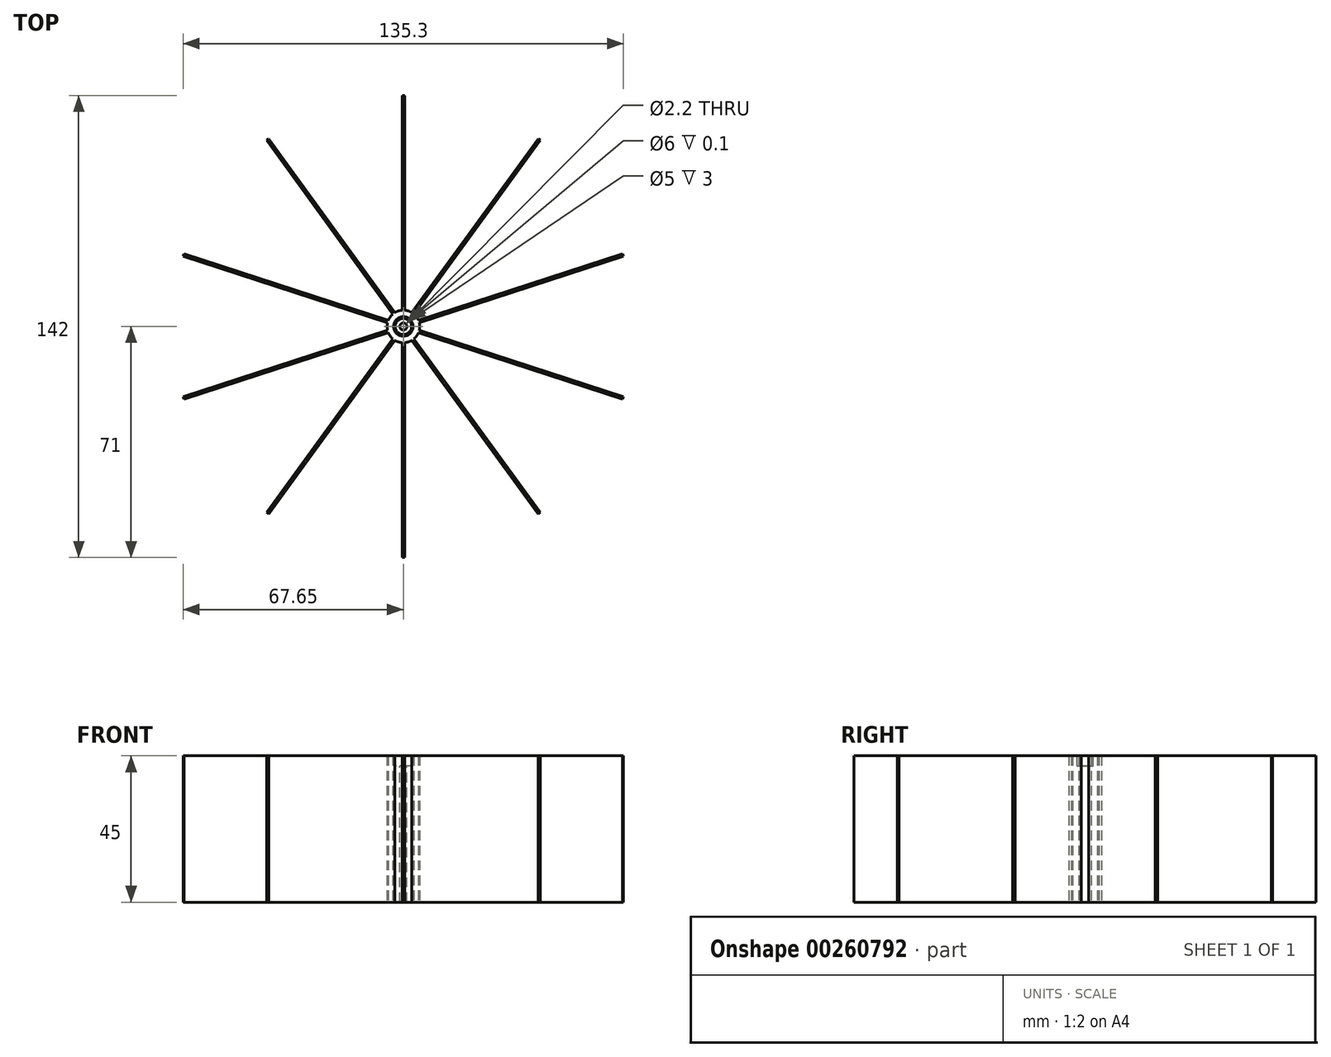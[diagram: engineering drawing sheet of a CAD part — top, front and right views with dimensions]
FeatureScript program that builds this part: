
annotation { "Feature Type Name" : "Feature", "Feature Type Description" : "" }
export const myFeature = defineFeature(function(context is Context, id is Id, definition is map)
    precondition{}
    {
        {
            var Q0;
            Q0=qCreatedBy(makeId("Top.planeOp"),FACE);
            var sketch = newSketch(context, id + "F0", { "sketchPlane" : qUnion([Q0])});
            skCircle(sketch, "E0", {"center": v(0, 0) * mm, "radius": 5 * mm});
            skLineSegment(sketch, "E1.bottom", {"start": v(-0.4, 0) * mm, "end": v(0.4, 0) * mm});
            skLineSegment(sketch, "E1.top", {"start": v(-0.4, 71) * mm, "end": v(0.4, 71) * mm});
            skLineSegment(sketch, "E1.left", {"start": v(-0.4, 0) * mm, "end": v(-0.4, 71) * mm});
            skLineSegment(sketch, "E1.right", {"start": v(0.4, 0) * mm, "end": v(0.4, 71) * mm});
            skLineSegment(sketch, "E2.1.0", {"start": v(-42.06, 57.2) * mm, "end": v(-41.4, 57.68) * mm});
            skLineSegment(sketch, "E2.1.1", {"start": v(-0.32, -0.24) * mm, "end": v(-42.06, 57.2) * mm});
            skLineSegment(sketch, "E2.1.2", {"start": v(0.32, 0.24) * mm, "end": v(-41.4, 57.68) * mm});
            skLineSegment(sketch, "E2.1.3", {"start": v(-0.32, -0.24) * mm, "end": v(0.32, 0.24) * mm});
            skLineSegment(sketch, "E2.2.0", {"start": v(-67.65, 21.56) * mm, "end": v(-67.4, 22.32) * mm});
            skLineSegment(sketch, "E2.2.1", {"start": v(-0.12, -0.38) * mm, "end": v(-67.65, 21.56) * mm});
            skLineSegment(sketch, "E2.2.2", {"start": v(0.12, 0.38) * mm, "end": v(-67.4, 22.32) * mm});
            skLineSegment(sketch, "E2.2.3", {"start": v(-0.12, -0.38) * mm, "end": v(0.12, 0.38) * mm});
            skLineSegment(sketch, "E2.3.0", {"start": v(-67.4, -22.32) * mm, "end": v(-67.65, -21.56) * mm});
            skLineSegment(sketch, "E2.3.1", {"start": v(0.12, -0.38) * mm, "end": v(-67.4, -22.32) * mm});
            skLineSegment(sketch, "E2.3.2", {"start": v(-0.12, 0.38) * mm, "end": v(-67.65, -21.56) * mm});
            skLineSegment(sketch, "E2.3.3", {"start": v(0.12, -0.38) * mm, "end": v(-0.12, 0.38) * mm});
            skLineSegment(sketch, "E2.4.0", {"start": v(-41.4, -57.68) * mm, "end": v(-42.06, -57.2) * mm});
            skLineSegment(sketch, "E2.4.1", {"start": v(0.32, -0.24) * mm, "end": v(-41.4, -57.68) * mm});
            skLineSegment(sketch, "E2.4.2", {"start": v(-0.32, 0.24) * mm, "end": v(-42.06, -57.2) * mm});
            skLineSegment(sketch, "E2.4.3", {"start": v(0.32, -0.24) * mm, "end": v(-0.32, 0.24) * mm});
            skLineSegment(sketch, "E2.5.0", {"start": v(0.4, -71) * mm, "end": v(-0.4, -71) * mm});
            skLineSegment(sketch, "E2.5.1", {"start": v(0.4, 0) * mm, "end": v(0.4, -71) * mm});
            skLineSegment(sketch, "E2.5.2", {"start": v(-0.4, 0) * mm, "end": v(-0.4, -71) * mm});
            skLineSegment(sketch, "E2.5.3", {"start": v(0.4, 0) * mm, "end": v(-0.4, 0) * mm});
            skLineSegment(sketch, "E2.6.0", {"start": v(42.06, -57.2) * mm, "end": v(41.4, -57.68) * mm});
            skLineSegment(sketch, "E2.6.1", {"start": v(0.32, 0.24) * mm, "end": v(42.06, -57.2) * mm});
            skLineSegment(sketch, "E2.6.2", {"start": v(-0.32, -0.24) * mm, "end": v(41.4, -57.68) * mm});
            skLineSegment(sketch, "E2.6.3", {"start": v(0.32, 0.24) * mm, "end": v(-0.32, -0.24) * mm});
            skLineSegment(sketch, "E2.7.0", {"start": v(67.65, -21.56) * mm, "end": v(67.4, -22.32) * mm});
            skLineSegment(sketch, "E2.7.1", {"start": v(0.12, 0.38) * mm, "end": v(67.65, -21.56) * mm});
            skLineSegment(sketch, "E2.7.2", {"start": v(-0.12, -0.38) * mm, "end": v(67.4, -22.32) * mm});
            skLineSegment(sketch, "E2.7.3", {"start": v(0.12, 0.38) * mm, "end": v(-0.12, -0.38) * mm});
            skLineSegment(sketch, "E3.1.8.0", {"start": v(67.4, 22.32) * mm, "end": v(67.65, 21.56) * mm});
            skLineSegment(sketch, "E3.3.8.0", {"start": v(-0.12, 0.38) * mm, "end": v(67.4, 22.32) * mm});
            skLineSegment(sketch, "E3.6.8.0", {"start": v(0.12, -0.38) * mm, "end": v(67.65, 21.56) * mm});
            skLineSegment(sketch, "E3.9.8.0", {"start": v(-0.12, 0.38) * mm, "end": v(0.12, -0.38) * mm});
            skLineSegment(sketch, "E3.1.9.0", {"start": v(41.4, 57.68) * mm, "end": v(42.06, 57.2) * mm});
            skLineSegment(sketch, "E3.3.9.0", {"start": v(-0.32, 0.24) * mm, "end": v(41.4, 57.68) * mm});
            skLineSegment(sketch, "E3.6.9.0", {"start": v(0.32, -0.24) * mm, "end": v(42.06, 57.2) * mm});
            skLineSegment(sketch, "E3.9.9.0", {"start": v(-0.32, 0.24) * mm, "end": v(0.32, -0.24) * mm});
            skSolve(sketch);
        }
        {
            var Q0;
            Q0 = qSketchRegion(id + "F0", true);
            extrude(context, id + "F1", {"entities" : qUnion([Q0]), "depth" : 45 * mm});
        }
        {
            var Q0;
            Q0=makeQuery(id+"F1.opExtrude","CAP_FACE",FACE,{"disambiguationData":[OSD([sQuery(id+"F0.wireOp",EDGE,"E0"),sQuery(id+"F0.wireOp",EDGE,"E1.top"),sQuery(id+"F0.wireOp",EDGE,"E1.left"),sQuery(id+"F0.wireOp",EDGE,"E1.right"),sQuery(id+"F0.wireOp",EDGE,"E2.1.0"),sQuery(id+"F0.wireOp",EDGE,"E2.1.1"),sQuery(id+"F0.wireOp",EDGE,"E2.1.2"),sQuery(id+"F0.wireOp",EDGE,"E2.2.0"),sQuery(id+"F0.wireOp",EDGE,"E2.2.1"),sQuery(id+"F0.wireOp",EDGE,"E2.2.2"),sQuery(id+"F0.wireOp",EDGE,"E2.3.0"),sQuery(id+"F0.wireOp",EDGE,"E2.3.1"),sQuery(id+"F0.wireOp",EDGE,"E2.3.2"),sQuery(id+"F0.wireOp",EDGE,"E2.4.0"),sQuery(id+"F0.wireOp",EDGE,"E2.4.1"),sQuery(id+"F0.wireOp",EDGE,"E2.4.2"),sQuery(id+"F0.wireOp",EDGE,"E2.5.0"),sQuery(id+"F0.wireOp",EDGE,"E2.5.1"),sQuery(id+"F0.wireOp",EDGE,"E2.5.2"),sQuery(id+"F0.wireOp",EDGE,"E2.6.0"),sQuery(id+"F0.wireOp",EDGE,"E2.6.1"),sQuery(id+"F0.wireOp",EDGE,"E2.6.2"),sQuery(id+"F0.wireOp",EDGE,"E2.7.0"),sQuery(id+"F0.wireOp",EDGE,"E2.7.1"),sQuery(id+"F0.wireOp",EDGE,"E2.7.2"),sQuery(id+"F0.wireOp",EDGE,"E3.1.8.0"),sQuery(id+"F0.wireOp",EDGE,"E3.3.8.0"),sQuery(id+"F0.wireOp",EDGE,"E3.6.8.0"),sQuery(id+"F0.wireOp",EDGE,"E3.1.9.0"),sQuery(id+"F0.wireOp",EDGE,"E3.3.9.0"),sQuery(id+"F0.wireOp",EDGE,"E3.6.9.0")])],"isStart":true});
            var sketch = newSketch(context, id + "F2", { "sketchPlane" : qUnion([Q0])});
            skLineSegment(sketch, "E4", {"start": v(0, 0.68) * mm, "end": v(0.4, 1.23) * mm});
            skLineSegment(sketch, "E5", {"start": v(0.4, 1.23) * mm, "end": v(0.4, 0.55) * mm});
            skLineSegment(sketch, "E6", {"start": v(0.4, 0.55) * mm, "end": v(1.05, 0.76) * mm});
            skLineSegment(sketch, "E7", {"start": v(1.05, 0.76) * mm, "end": v(0.65, 0.21) * mm});
            skLineSegment(sketch, "E8", {"start": v(0.65, 0.21) * mm, "end": v(1.3, 0) * mm});
            skLineSegment(sketch, "E9", {"start": v(1.3, 0) * mm, "end": v(0.65, -0.21) * mm});
            skLineSegment(sketch, "E10", {"start": v(0.65, -0.21) * mm, "end": v(1.05, -0.76) * mm});
            skLineSegment(sketch, "E11", {"start": v(1.05, -0.76) * mm, "end": v(0.4, -0.55) * mm});
            skLineSegment(sketch, "E12", {"start": v(0.4, -0.55) * mm, "end": v(0.4, -1.23) * mm});
            skLineSegment(sketch, "E13", {"start": v(0.4, -1.23) * mm, "end": v(0, -0.68) * mm});
            skLineSegment(sketch, "E14", {"start": v(0, -0.68) * mm, "end": v(-0.4, -1.23) * mm});
            skLineSegment(sketch, "E15", {"start": v(-0.4, -1.23) * mm, "end": v(-0.4, -0.55) * mm});
            skLineSegment(sketch, "E16", {"start": v(-0.4, -0.55) * mm, "end": v(-1.05, -0.76) * mm});
            skLineSegment(sketch, "E17", {"start": v(-1.05, -0.76) * mm, "end": v(-0.65, -0.21) * mm});
            skLineSegment(sketch, "E18", {"start": v(-0.65, -0.21) * mm, "end": v(-1.3, 0) * mm});
            skLineSegment(sketch, "E19", {"start": v(-1.3, 0) * mm, "end": v(-0.65, 0.21) * mm});
            skLineSegment(sketch, "E20", {"start": v(-0.65, 0.21) * mm, "end": v(-1.05, 0.76) * mm});
            skLineSegment(sketch, "E21", {"start": v(-1.05, 0.76) * mm, "end": v(-0.4, 0.55) * mm});
            skLineSegment(sketch, "E22", {"start": v(-0.4, 0.55) * mm, "end": v(-0.4, 1.23) * mm});
            skLineSegment(sketch, "E23", {"start": v(-0.4, 1.23) * mm, "end": v(0, 0.68) * mm});
            skSolve(sketch);
        }
        {
            var Q0;
            Q0 = qSketchRegion(id + "F2", true);
            extrude(context, id + "F3", {"entities" : qUnion([Q0]), "operationType" : NewBodyOperationType.ADD, "oppositeDirection" : true, "depth" : 45 * mm});
        }
        {
            var Q0;
            Q0=makeQuery(id+"F3.boolean.opBoolean","MERGE",FACE,{"derivedFrom":[makeQuery(id+"F1.opExtrude","CAP_FACE",FACE,{"disambiguationData":[OSD([sQuery(id+"F0.wireOp",EDGE,"E0"),sQuery(id+"F0.wireOp",EDGE,"E1.top"),sQuery(id+"F0.wireOp",EDGE,"E1.left"),sQuery(id+"F0.wireOp",EDGE,"E1.right"),sQuery(id+"F0.wireOp",EDGE,"E2.1.0"),sQuery(id+"F0.wireOp",EDGE,"E2.1.1"),sQuery(id+"F0.wireOp",EDGE,"E2.1.2"),sQuery(id+"F0.wireOp",EDGE,"E2.2.0"),sQuery(id+"F0.wireOp",EDGE,"E2.2.1"),sQuery(id+"F0.wireOp",EDGE,"E2.2.2"),sQuery(id+"F0.wireOp",EDGE,"E2.3.0"),sQuery(id+"F0.wireOp",EDGE,"E2.3.1"),sQuery(id+"F0.wireOp",EDGE,"E2.3.2"),sQuery(id+"F0.wireOp",EDGE,"E2.4.0"),sQuery(id+"F0.wireOp",EDGE,"E2.4.1"),sQuery(id+"F0.wireOp",EDGE,"E2.4.2"),sQuery(id+"F0.wireOp",EDGE,"E2.5.0"),sQuery(id+"F0.wireOp",EDGE,"E2.5.1"),sQuery(id+"F0.wireOp",EDGE,"E2.5.2"),sQuery(id+"F0.wireOp",EDGE,"E2.6.0"),sQuery(id+"F0.wireOp",EDGE,"E2.6.1"),sQuery(id+"F0.wireOp",EDGE,"E2.6.2"),sQuery(id+"F0.wireOp",EDGE,"E2.7.0"),sQuery(id+"F0.wireOp",EDGE,"E2.7.1"),sQuery(id+"F0.wireOp",EDGE,"E2.7.2"),sQuery(id+"F0.wireOp",EDGE,"E3.1.8.0"),sQuery(id+"F0.wireOp",EDGE,"E3.3.8.0"),sQuery(id+"F0.wireOp",EDGE,"E3.6.8.0"),sQuery(id+"F0.wireOp",EDGE,"E3.1.9.0"),sQuery(id+"F0.wireOp",EDGE,"E3.3.9.0"),sQuery(id+"F0.wireOp",EDGE,"E3.6.9.0")])],"isStart":false}),makeQuery(id+"F3.opExtrude","CAP_FACE",FACE,{"disambiguationData":[OSD([sQuery(id+"F2.wireOp",EDGE,"E4"),sQuery(id+"F2.wireOp",EDGE,"E5"),sQuery(id+"F2.wireOp",EDGE,"E6"),sQuery(id+"F2.wireOp",EDGE,"E7"),sQuery(id+"F2.wireOp",EDGE,"E8"),sQuery(id+"F2.wireOp",EDGE,"E9"),sQuery(id+"F2.wireOp",EDGE,"E10"),sQuery(id+"F2.wireOp",EDGE,"E11"),sQuery(id+"F2.wireOp",EDGE,"E12"),sQuery(id+"F2.wireOp",EDGE,"E13"),sQuery(id+"F2.wireOp",EDGE,"E14"),sQuery(id+"F2.wireOp",EDGE,"E15"),sQuery(id+"F2.wireOp",EDGE,"E16"),sQuery(id+"F2.wireOp",EDGE,"E17"),sQuery(id+"F2.wireOp",EDGE,"E18"),sQuery(id+"F2.wireOp",EDGE,"E19"),sQuery(id+"F2.wireOp",EDGE,"E20"),sQuery(id+"F2.wireOp",EDGE,"E21"),sQuery(id+"F2.wireOp",EDGE,"E22"),sQuery(id+"F2.wireOp",EDGE,"E23")])],"isStart":false})]});
            var sketch = newSketch(context, id + "F4", { "sketchPlane" : qUnion([Q0])});
            skCircle(sketch, "E24", {"center": v(0, 0) * mm, "radius": 1.1 * mm});
            skSolve(sketch);
        }
        {
            var Q0;
            Q0=makeQuery(id+"F4.imprint","IMPRINT",FACE,{"disambiguationData":[TD([[makeQuery(id+"F4.imprint","IMPRINT",EDGE,{"derivedFrom":sQuery(id+"F4.wireOp",EDGE,"E24")}),1.0]])]});
            var Q1;
            Q1=sQuery(id+"F4.wireOp",EDGE,"E24");
            extrude(context, id + "F5", {"entities" : qUnion([Q0]), "operationType" : NewBodyOperationType.REMOVE, "surfaceEntities" : qUnion([Q1]), "endBound" : BoundingType.UP_TO_NEXT, "oppositeDirection" : true, "depth" : 25 * mm});
        }
        {
            var Q0;
            Q0=makeQuery(id+"F3.boolean.opBoolean","MERGE",FACE,{"derivedFrom":[makeQuery(id+"F1.opExtrude","CAP_FACE",FACE,{"disambiguationData":[OSD([sQuery(id+"F0.wireOp",EDGE,"E0"),sQuery(id+"F0.wireOp",EDGE,"E1.top"),sQuery(id+"F0.wireOp",EDGE,"E1.left"),sQuery(id+"F0.wireOp",EDGE,"E1.right"),sQuery(id+"F0.wireOp",EDGE,"E2.1.0"),sQuery(id+"F0.wireOp",EDGE,"E2.1.1"),sQuery(id+"F0.wireOp",EDGE,"E2.1.2"),sQuery(id+"F0.wireOp",EDGE,"E2.2.0"),sQuery(id+"F0.wireOp",EDGE,"E2.2.1"),sQuery(id+"F0.wireOp",EDGE,"E2.2.2"),sQuery(id+"F0.wireOp",EDGE,"E2.3.0"),sQuery(id+"F0.wireOp",EDGE,"E2.3.1"),sQuery(id+"F0.wireOp",EDGE,"E2.3.2"),sQuery(id+"F0.wireOp",EDGE,"E2.4.0"),sQuery(id+"F0.wireOp",EDGE,"E2.4.1"),sQuery(id+"F0.wireOp",EDGE,"E2.4.2"),sQuery(id+"F0.wireOp",EDGE,"E2.5.0"),sQuery(id+"F0.wireOp",EDGE,"E2.5.1"),sQuery(id+"F0.wireOp",EDGE,"E2.5.2"),sQuery(id+"F0.wireOp",EDGE,"E2.6.0"),sQuery(id+"F0.wireOp",EDGE,"E2.6.1"),sQuery(id+"F0.wireOp",EDGE,"E2.6.2"),sQuery(id+"F0.wireOp",EDGE,"E2.7.0"),sQuery(id+"F0.wireOp",EDGE,"E2.7.1"),sQuery(id+"F0.wireOp",EDGE,"E2.7.2"),sQuery(id+"F0.wireOp",EDGE,"E3.1.8.0"),sQuery(id+"F0.wireOp",EDGE,"E3.3.8.0"),sQuery(id+"F0.wireOp",EDGE,"E3.6.8.0"),sQuery(id+"F0.wireOp",EDGE,"E3.1.9.0"),sQuery(id+"F0.wireOp",EDGE,"E3.3.9.0"),sQuery(id+"F0.wireOp",EDGE,"E3.6.9.0")])],"isStart":false}),makeQuery(id+"F3.opExtrude","CAP_FACE",FACE,{"disambiguationData":[OSD([sQuery(id+"F2.wireOp",EDGE,"E4"),sQuery(id+"F2.wireOp",EDGE,"E5"),sQuery(id+"F2.wireOp",EDGE,"E6"),sQuery(id+"F2.wireOp",EDGE,"E7"),sQuery(id+"F2.wireOp",EDGE,"E8"),sQuery(id+"F2.wireOp",EDGE,"E9"),sQuery(id+"F2.wireOp",EDGE,"E10"),sQuery(id+"F2.wireOp",EDGE,"E11"),sQuery(id+"F2.wireOp",EDGE,"E12"),sQuery(id+"F2.wireOp",EDGE,"E13"),sQuery(id+"F2.wireOp",EDGE,"E14"),sQuery(id+"F2.wireOp",EDGE,"E15"),sQuery(id+"F2.wireOp",EDGE,"E16"),sQuery(id+"F2.wireOp",EDGE,"E17"),sQuery(id+"F2.wireOp",EDGE,"E18"),sQuery(id+"F2.wireOp",EDGE,"E19"),sQuery(id+"F2.wireOp",EDGE,"E20"),sQuery(id+"F2.wireOp",EDGE,"E21"),sQuery(id+"F2.wireOp",EDGE,"E22"),sQuery(id+"F2.wireOp",EDGE,"E23")])],"isStart":false})]});
            var sketch = newSketch(context, id + "F6", { "sketchPlane" : qUnion([Q0])});
            skCircle(sketch, "E25", {"center": v(0, 0) * mm, "radius": 3 * mm});
            skSolve(sketch);
        }
        {
            var Q0;
            Q0 = qSketchRegion(id + "F6", true);
            extrude(context, id + "F7", {"entities" : qUnion([Q0]), "operationType" : NewBodyOperationType.REMOVE, "oppositeDirection" : true, "depth" : 0.1 * mm});
        }
        {
            var Q0;
            Q0=makeQuery(id+"F7.boolean.opBoolean","COPY",FACE,{"derivedFrom":makeQuery(id+"F7.opExtrude","CAP_FACE",FACE,{"disambiguationData":[OSD([sQuery(id+"F6.wireOp",EDGE,"E25")])],"isStart":false})});
            var sketch = newSketch(context, id + "F8", { "sketchPlane" : qUnion([Q0])});
            skCircle(sketch, "E26", {"center": v(0, 0) * mm, "radius": 2.5 * mm});
            skSolve(sketch);
        }
        {
            var Q0;
            Q0 = qSketchRegion(id + "F8", true);
            extrude(context, id + "F9", {"entities" : qUnion([Q0]), "operationType" : NewBodyOperationType.REMOVE, "oppositeDirection" : true, "depth" : 3 * mm});
        }
    });
